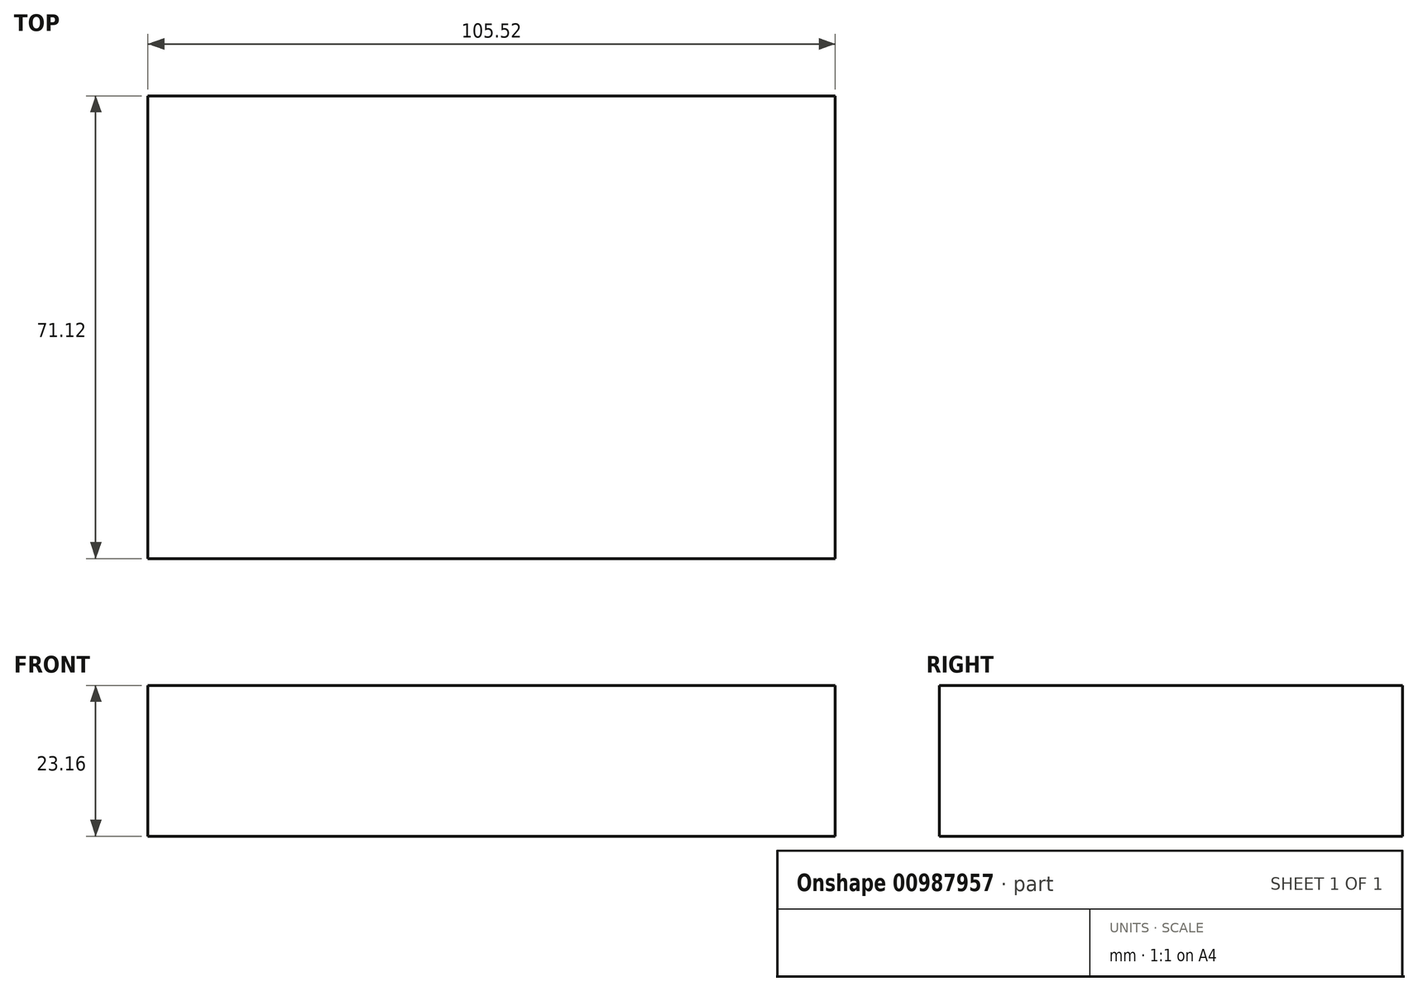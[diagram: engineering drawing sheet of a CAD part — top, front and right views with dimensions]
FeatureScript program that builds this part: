
annotation { "Feature Type Name" : "Feature", "Feature Type Description" : "" }
export const myFeature = defineFeature(function(context is Context, id is Id, definition is map)
    precondition{}
    {
        {
            var Q0;
            Q0=qCreatedBy(makeId("Front.planeOp"),FACE);
            var sketch = newSketch(context, id + "F0", { "sketchPlane" : qUnion([Q0])});
            skLineSegment(sketch, "E0.bottom", {"start": v(52.76, 11.58) * mm, "end": v(-52.76, 11.58) * mm});
            skLineSegment(sketch, "E0.top", {"start": v(52.76, -11.58) * mm, "end": v(-52.76, -11.58) * mm});
            skLineSegment(sketch, "E0.left", {"start": v(52.76, 11.58) * mm, "end": v(52.76, -11.58) * mm});
            skLineSegment(sketch, "E0.right", {"start": v(-52.76, 11.58) * mm, "end": v(-52.76, -11.58) * mm});
            skPoint(sketch, "E0.middle", {"position": v(0, 0) * mm});
            skSolve(sketch);
        }
        {
            var Q0;
            Q0=makeQuery(id+"F0.imprint","IMPRINT",FACE,{"disambiguationData":[TD([[makeQuery(id+"F0.imprint","IMPRINT",EDGE,{"derivedFrom":sQuery(id+"F0.wireOp",EDGE,"E0.bottom")}),1.0]])]});
            extrude(context, id + "F1", {"entities" : qUnion([Q0]), "endBound" : BoundingType.SYMMETRIC, "depth" : 71.12 * mm, "offsetDistance" : 25.4 * mm});
        }
    });
